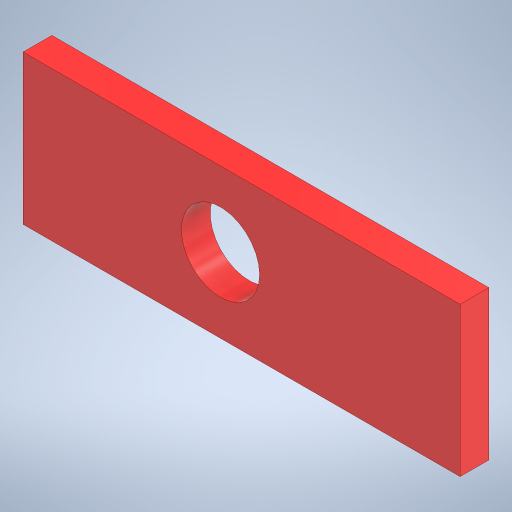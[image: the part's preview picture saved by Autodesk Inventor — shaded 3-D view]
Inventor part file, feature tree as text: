
AUTODESK INVENTOR PART (.ipt)
format: ipt  version: 2023 (Build 270158000, 158)  size: 197,120 bytes
history: native  units: mm
features: extrude x1, sketch x1
ambient origin geometry x8: Origin, YZ Plane, XZ Plane, XY Plane, X Axis, Y Axis, Z Axis, Center Point
bodies: Volumenkörper1 (feature_tree)
feature tree (2):
  extrude  "Extrusion1"  Depth=24.3mm
  sketch  "Skizze1"  dims[d0=8.3mm d1=24.3mm d2=4.15mm d3=4.15mm d4=4.35mm d5=13.325mm d6=1.6mm d7=0.0mm]
